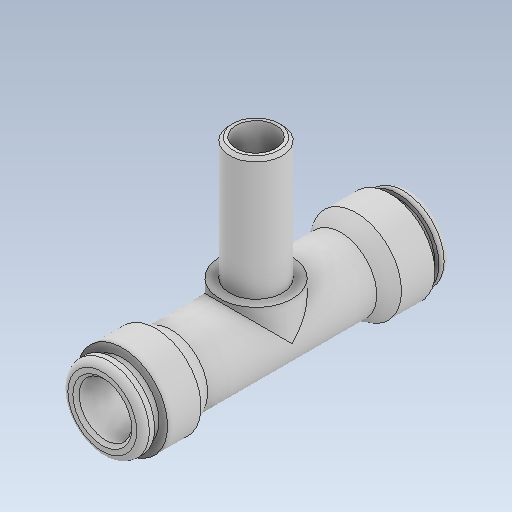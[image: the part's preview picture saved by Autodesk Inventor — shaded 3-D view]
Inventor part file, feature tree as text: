
AUTODESK INVENTOR PART (.ipt)
format: ipt  version: 2020 (Build 240168000, 168)  size: 201,728 bytes
history: native  units: in
note: dims shown in document units (in); Inventor stores cm internally (conversion verified against a paired STEP export)
features: chamfer x1
ambient origin geometry x8: Origin, YZ Plane, XZ Plane, XY Plane, X Axis, Y Axis, Z Axis, Center Point
bodies: Solid1 (feature_tree)
feature tree (1):
  chamfer  "Chamfer1"  [1 undecoded]
note: 1 required parameter value undecoded (feature->parameter linkage not recoverable at this tier; creation-order binding heuristic only, values carry confidence <= 0.55)
